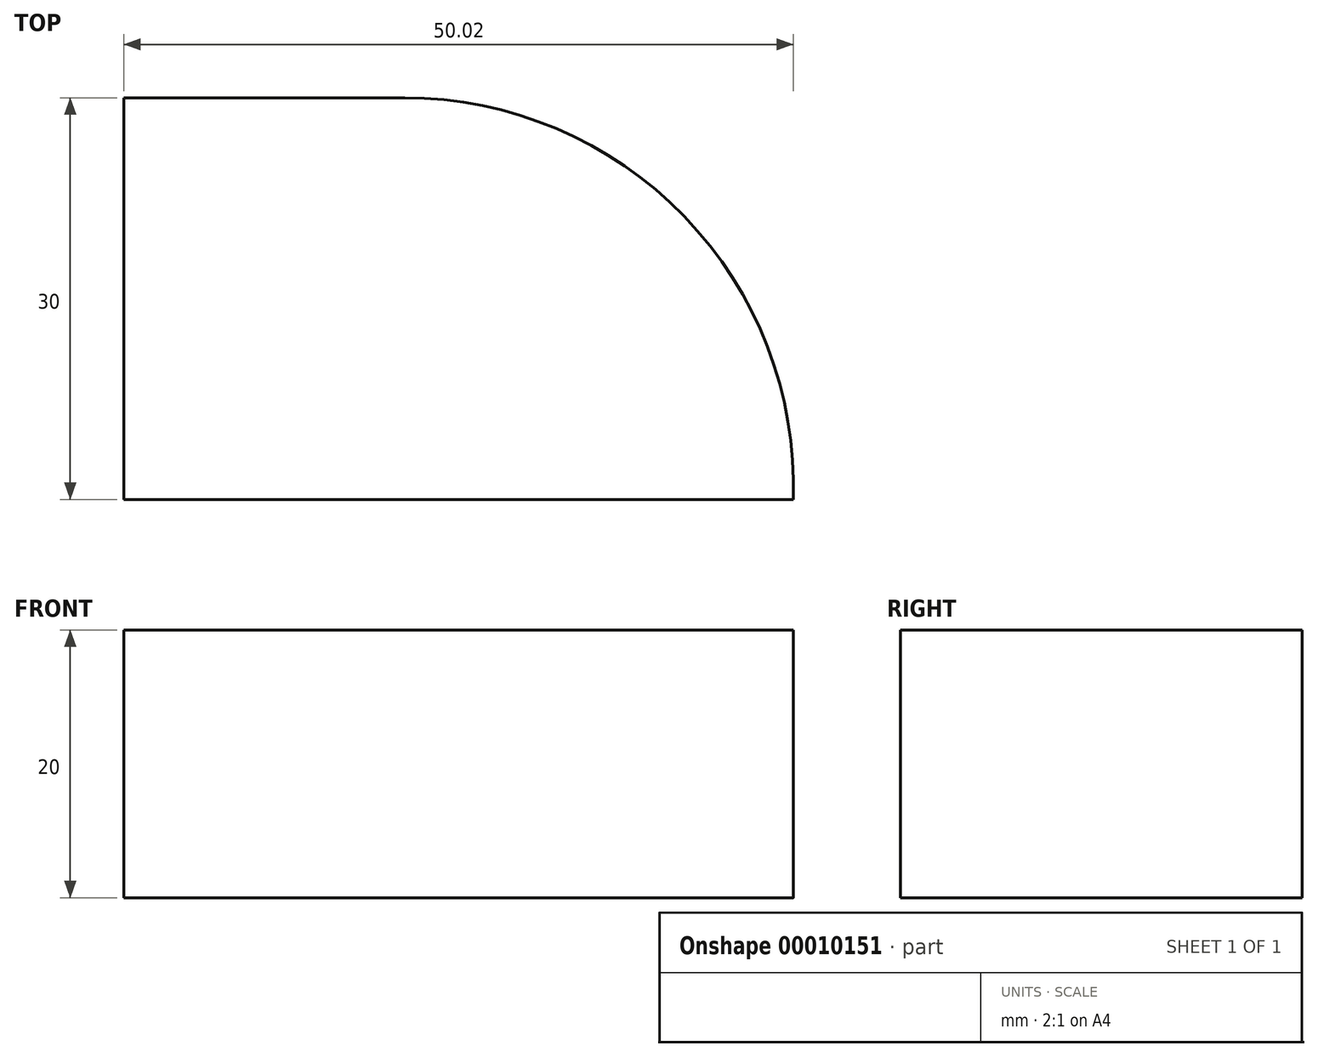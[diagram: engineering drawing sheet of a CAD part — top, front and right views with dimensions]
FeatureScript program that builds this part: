
annotation { "Feature Type Name" : "Feature", "Feature Type Description" : "" }
export const myFeature = defineFeature(function(context is Context, id is Id, definition is map)
    precondition{}
    {
        {
            var Q0;
            Q0=qCreatedBy(makeId("Top.planeOp"),FACE);
            var sketch = newSketch(context, id + "F0", { "sketchPlane" : qUnion([Q0])});
            skLineSegment(sketch, "E0", {"start": v(0, 0) * mm, "end": v(50, 0) * mm});
            skLineSegment(sketch, "E1", {"start": v(0, 0) * mm, "end": v(0, 30) * mm});
            skLineSegment(sketch, "E2", {"start": v(0, 30) * mm, "end": v(20.98, 30) * mm});
            skArc(sketch, "E3", {"start": v(50, 0) * mm, "mid": v(41.85, 21.15) * mm, "end": v(20.98, 30) * mm});
            skSolve(sketch);
        }
        {
            var Q0;
            Q0=makeQuery(id+"F0.imprint","IMPRINT",FACE,{"disambiguationData":[TD([[makeQuery(id+"F0.imprint","IMPRINT",EDGE,{"derivedFrom":sQuery(id+"F0.wireOp",EDGE,"E0")}),1.0]])]});
            extrude(context, id + "F1", {"entities" : qUnion([Q0]), "depth" : 20 * mm});
        }
    });
